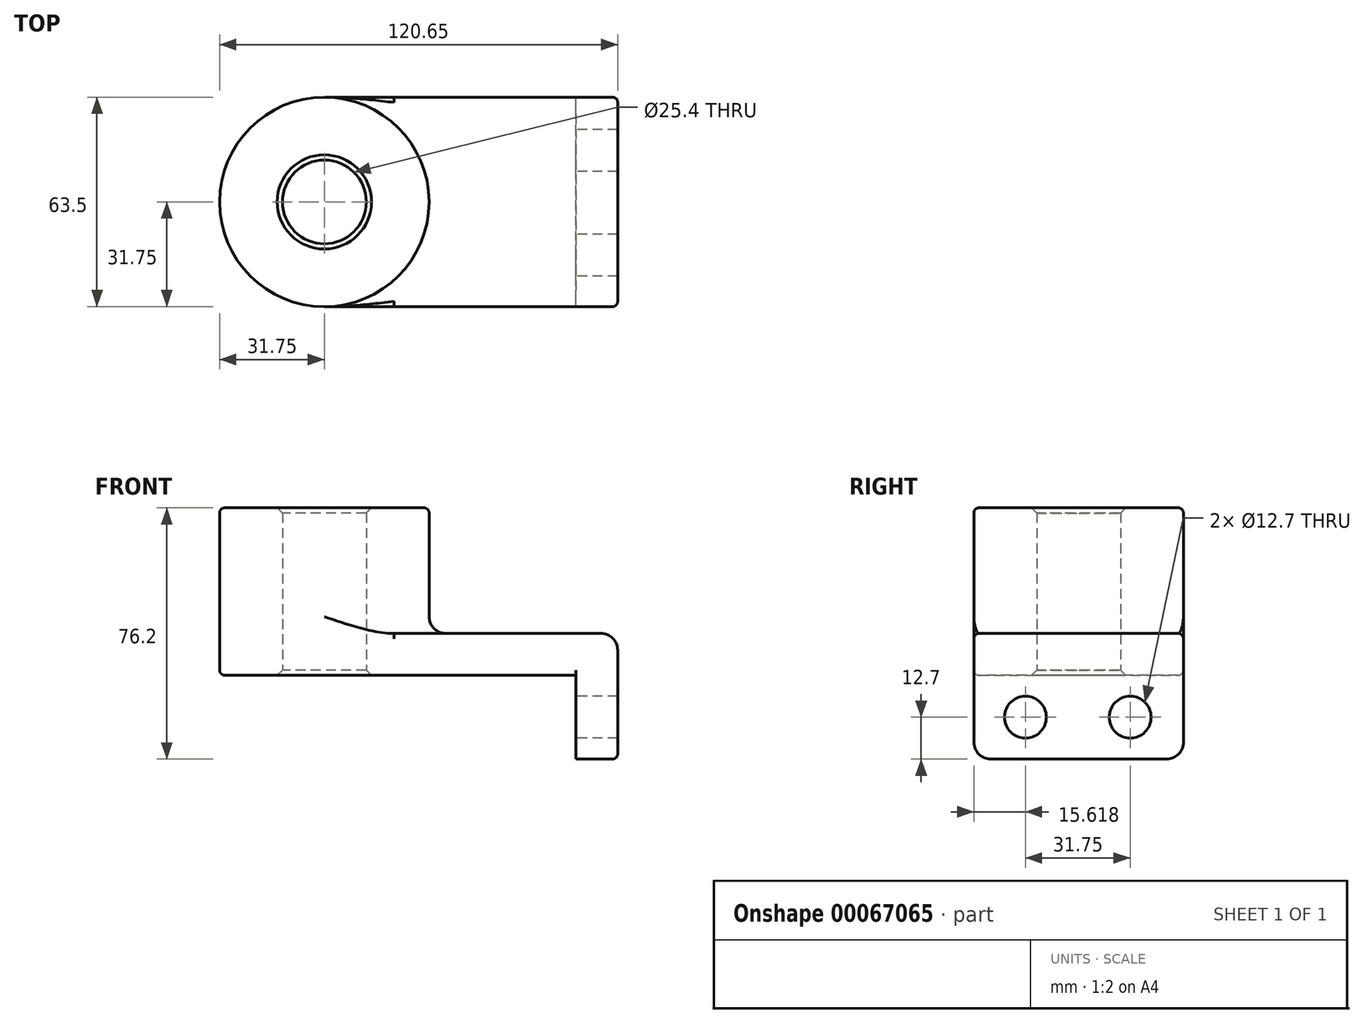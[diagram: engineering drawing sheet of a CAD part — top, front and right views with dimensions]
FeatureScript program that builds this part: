
annotation { "Feature Type Name" : "Feature", "Feature Type Description" : "" }
export const myFeature = defineFeature(function(context is Context, id is Id, definition is map)
    precondition{}
    {
        {
            var Q0;
            Q0=qCreatedBy(makeId("Top.planeOp"),FACE);
            var sketch = newSketch(context, id + "F0", { "sketchPlane" : qUnion([Q0])});
            skLineSegment(sketch, "E0.rect.bottom", {"start": v(38.1, -31.75) * mm, "end": v(-38.1, -31.75) * mm});
            skLineSegment(sketch, "E0.rect.top", {"start": v(38.1, 31.75) * mm, "end": v(-38.1, 31.75) * mm});
            skLineSegment(sketch, "E0.rect.left", {"start": v(38.1, -31.75) * mm, "end": v(38.1, 31.75) * mm});
            skLineSegment(sketch, "E0.rect.right", {"start": v(-38.1, -31.75) * mm, "end": v(-38.1, 31.75) * mm});
            skPoint(sketch, "E0.rect.middle", {"position": v(0, 0) * mm});
            skCircle(sketch, "E1", {"center": v(-38.1, 0) * mm, "radius": 31.75 * mm});
            skCircle(sketch, "E2", {"center": v(-38.1, 0) * mm, "radius": 12.7 * mm});
            skSolve(sketch);
        }
        {
            var Q0;
            {var subQ0=sQuery(id+"F0.wireOp",EDGE,"E0.rect.bottom");Q0=makeQuery(id+"F0.imprint","IMPRINT",FACE,{"disambiguationData":[TD([[makeQuery(id+"F0.imprint","IMPRINT",EDGE,{"derivedFrom":subQ0}),-1.0]])]});}
            var Q1;
            {var subQ1=sQuery(id+"F0.wireOp",EDGE,"E0.rect.right");var subQ3=sQuery(id+"F0.wireOp",EDGE,"E2");var subQ4=makeQuery(id+"F0.imprint","INTERSECT",VERTEX,{"disambiguationData":[OD(0.0)],"derivedFrom":[subQ1,subQ3]});Q1=makeQuery(id+"F0.imprint","IMPRINT",FACE,{"disambiguationData":[TD([[makeQuery(id+"F0.imprint","IMPRINT",EDGE,{"disambiguationData":[TD([[subQ4,1.0]])],"derivedFrom":subQ3}),-1.0]])]});}
            var Q2;
            {var subQ1=sQuery(id+"F0.wireOp",EDGE,"E0.rect.right");var subQ3=sQuery(id+"F0.wireOp",EDGE,"E2");var subQ4=makeQuery(id+"F0.imprint","INTERSECT",VERTEX,{"disambiguationData":[OD(0.0)],"derivedFrom":[subQ1,subQ3]});Q2=makeQuery(id+"F0.imprint","IMPRINT",FACE,{"disambiguationData":[TD([[makeQuery(id+"F0.imprint","IMPRINT",EDGE,{"disambiguationData":[TD([[subQ4,-1.0]])],"derivedFrom":subQ3}),-1.0]])]});}
            extrude(context, id + "F1", {"entities" : qUnion([Q0, Q1, Q2]), "depth" : 12.7 * mm});
        }
        {
            var Q0;
            {var subQ1=sQuery(id+"F0.wireOp",EDGE,"E0.rect.right");var subQ3=sQuery(id+"F0.wireOp",EDGE,"E2");var subQ4=makeQuery(id+"F0.imprint","INTERSECT",VERTEX,{"disambiguationData":[OD(0.0)],"derivedFrom":[subQ1,subQ3]});Q0=makeQuery(id+"F0.imprint","IMPRINT",FACE,{"disambiguationData":[TD([[makeQuery(id+"F0.imprint","IMPRINT",EDGE,{"disambiguationData":[TD([[subQ4,-1.0]])],"derivedFrom":subQ3}),-1.0]])]});}
            var Q1;
            {var subQ1=sQuery(id+"F0.wireOp",EDGE,"E0.rect.right");var subQ3=sQuery(id+"F0.wireOp",EDGE,"E2");var subQ4=makeQuery(id+"F0.imprint","INTERSECT",VERTEX,{"disambiguationData":[OD(0.0)],"derivedFrom":[subQ1,subQ3]});Q1=makeQuery(id+"F0.imprint","IMPRINT",FACE,{"disambiguationData":[TD([[makeQuery(id+"F0.imprint","IMPRINT",EDGE,{"disambiguationData":[TD([[subQ4,1.0]])],"derivedFrom":subQ3}),-1.0]])]});}
            extrude(context, id + "F2", {"entities" : qUnion([Q0, Q1]), "operationType" : NewBodyOperationType.ADD, "depth" : 50.8 * mm});
        }
        {
            var Q0;
            Q0=makeQuery(id+"F1.opExtrude","SWEPT_FACE",FACE,{"disambiguationData":[OSD([sQuery(id+"F0.wireOp",EDGE,"E0.rect.left")])]});
            var sketch = newSketch(context, id + "F3", { "sketchPlane" : qUnion([Q0])});
            skLineSegment(sketch, "E3.bottom", {"start": v(31.75, 12.7) * mm, "end": v(-31.75, 12.7) * mm});
            skLineSegment(sketch, "E3.top", {"start": v(31.75, -25.4) * mm, "end": v(-31.75, -25.4) * mm});
            skLineSegment(sketch, "E3.left", {"start": v(31.75, 12.7) * mm, "end": v(31.75, -25.4) * mm});
            skLineSegment(sketch, "E3.right", {"start": v(-31.75, 12.7) * mm, "end": v(-31.75, -25.4) * mm});
            skLineSegment(sketch, "E4", {"start": v(0, 0) * mm, "end": v(0, -25.4) * mm, "construction": true});
            skCircle(sketch, "E5", {"center": v(-16.13, -12.7) * mm, "radius": 6.35 * mm});
            skCircle(sketch, "E6", {"center": v(15.62, -12.7) * mm, "radius": 6.35 * mm});
            skSolve(sketch);
        }
        {
            var Q0;
            {var subQ2=sQuery(id+"F3.wireOp",EDGE,"E3.top");Q0=makeQuery(id+"F3.imprint","IMPRINT",FACE,{"disambiguationData":[TD([[makeQuery(id+"F3.imprint","IMPRINT",EDGE,{"derivedFrom":subQ2}),-1.0]])]});}
            var Q1;
            {var subQ0=sQuery(id+"F3.wireOp",EDGE,"E3.bottom");Q1=makeQuery(id+"F3.imprint","IMPRINT",FACE,{"disambiguationData":[TD([[makeQuery(id+"F3.imprint","IMPRINT",EDGE,{"derivedFrom":subQ0}),-1.0]])]});}
            extrude(context, id + "F4", {"entities" : qUnion([Q0, Q1]), "operationType" : NewBodyOperationType.ADD, "depth" : 12.7 * mm});
        }
        {
            var Q0;
            Q0=makeQuery(id+"F4.opExtrude","SWEPT_EDGE",EDGE,{"disambiguationData":[OSD([sQuery(id+"F3.wireOp",EDGE,"E3.top"),sQuery(id+"F3.wireOp",EDGE,"E3.right")])]});
            var Q1;
            {var subQ0=sQuery(id+"F0.wireOp",EDGE,"E1");Q1=makeQuery(id+"F2.boolean.opBoolean","INTERSECT",EDGE,{"derivedFrom":[makeQuery(id+"F1.opExtrude","CAP_FACE",FACE,{"disambiguationData":[OSD([sQuery(id+"F0.wireOp",EDGE,"E0.rect.bottom"),sQuery(id+"F0.wireOp",EDGE,"E0.rect.top"),sQuery(id+"F0.wireOp",EDGE,"E0.rect.left"),subQ0,sQuery(id+"F0.wireOp",EDGE,"E2")])],"isStart":false}),makeQuery(id+"F2.opExtrude","SWEPT_FACE",FACE,{"disambiguationData":[OSD([subQ0])]})]});}
            var Q2;
            Q2=makeQuery(id+"F4.opExtrude","CAP_EDGE",EDGE,{"disambiguationData":[OSD([sQuery(id+"F3.wireOp",EDGE,"E3.bottom")])],"isStart":false});
            var Q3;
            Q3=makeQuery(id+"F4.opExtrude","SWEPT_EDGE",EDGE,{"disambiguationData":[OSD([sQuery(id+"F3.wireOp",EDGE,"E3.top"),sQuery(id+"F3.wireOp",EDGE,"E3.left")])]});
            var Q4;
            Q4=makeQuery(id+"F1.opExtrude","CAP_EDGE",EDGE,{"disambiguationData":[OSD([sQuery(id+"F0.wireOp",EDGE,"E0.rect.left")])],"isStart":true});
            fillet(context, id + "F5", {"entities" : qUnion([Q0, Q1, Q2, Q3, Q4]), "radius" : 5.08 * mm, "tangentPropagation" : true, "allowEdgeOverflow" : false});
        }
        {
            var Q0;
            Q0=makeQuery(id+"F4.boolean.opBoolean","MERGE",EDGE,{"derivedFrom":[makeQuery(id+"F1.opExtrude","CAP_EDGE",EDGE,{"disambiguationData":[OSD([sQuery(id+"F0.wireOp",EDGE,"E0.rect.bottom")])],"isStart":false}),makeQuery(id+"F4.opExtrude","SWEPT_EDGE",EDGE,{"disambiguationData":[OSD([sQuery(id+"F3.wireOp",EDGE,"E3.bottom"),sQuery(id+"F3.wireOp",EDGE,"E3.right")])]})]});
            var Q1;
            Q1=makeQuery(id+"F4.boolean.opBoolean","MERGE",EDGE,{"derivedFrom":[makeQuery(id+"F1.opExtrude","CAP_EDGE",EDGE,{"disambiguationData":[OSD([sQuery(id+"F0.wireOp",EDGE,"E0.rect.top")])],"isStart":false}),makeQuery(id+"F4.opExtrude","SWEPT_EDGE",EDGE,{"disambiguationData":[OSD([sQuery(id+"F3.wireOp",EDGE,"E3.bottom"),sQuery(id+"F3.wireOp",EDGE,"E3.left")])]})]});
            var Q2;
            Q2=makeQuery(id+"F1.opExtrude","CAP_EDGE",EDGE,{"disambiguationData":[OSD([sQuery(id+"F0.wireOp",EDGE,"E0.rect.bottom")])],"isStart":true});
            var Q3;
            Q3=makeQuery(id+"F1.opExtrude","CAP_EDGE",EDGE,{"disambiguationData":[OSD([sQuery(id+"F0.wireOp",EDGE,"E0.rect.top")])],"isStart":true});
            var Q4;
            Q4=makeQuery(id+"F2.opExtrude","CAP_EDGE",EDGE,{"disambiguationData":[OSD([sQuery(id+"F0.wireOp",EDGE,"E1")])],"isStart":false});
            fillet(context, id + "F6", {"entities" : qUnion([Q0, Q1, Q2, Q3, Q4]), "radius" : 1.59 * mm, "tangentPropagation" : true, "allowEdgeOverflow" : false});
        }
        {
            var Q0;
            {var subQ0=sQuery(id+"F0.wireOp",EDGE,"E2");Q0=makeQuery(id+"F2.boolean.opBoolean","MERGE",FACE,{"derivedFrom":[makeQuery(id+"F1.opExtrude","SWEPT_FACE",FACE,{"disambiguationData":[OSD([subQ0])]}),makeQuery(id+"F2.opExtrude","SWEPT_FACE",FACE,{"disambiguationData":[OSD([subQ0])]})]});}
            chamfer(context, id + "F7", {"entities" : qUnion([Q0]), "width" : 1.59 * mm, "tangentPropagation" : true});
        }
    });
